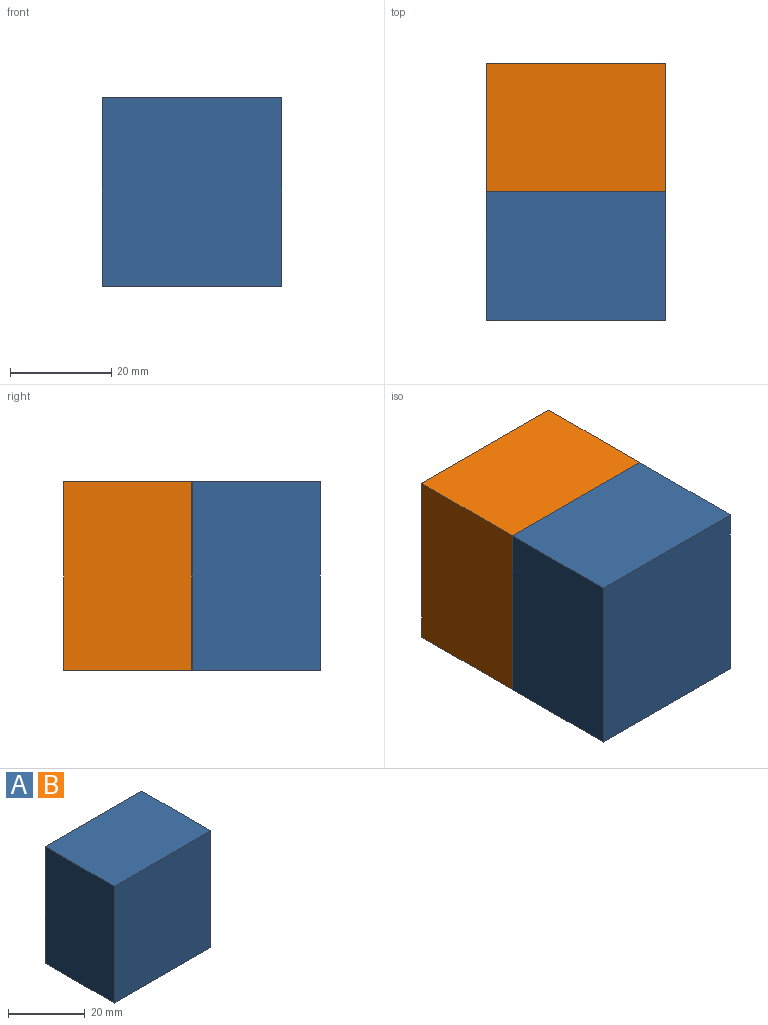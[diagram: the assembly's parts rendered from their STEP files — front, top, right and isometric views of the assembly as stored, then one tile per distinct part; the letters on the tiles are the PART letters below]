
ASSEMBLY  parts=2 mates=1
PART A: 6 faces, bbox 35.5x25.4x37.2 mm
  f0: plane 35.52x25.4mm, normal (0,0,-1), area 902.3mm2, adj f1,f3,f4,f5
  f1: plane 37.22x25.4mm, normal (1,0,0), area 945.4mm2, adj f0,f2,f4,f5
  f2: plane 35.52x25.4mm, normal (0,0,1), area 902.3mm2, adj f1,f3,f4,f5
  f3: plane 37.22x25.4mm, normal (-1,0,0), area 945.4mm2, adj f0,f2,f4,f5
  f4: plane 37.22x35.52mm, normal (0,-1,0), area 1322.2mm2, adj f0,f1,f2,f3
  f5: plane 37.22x35.52mm, normal (0,1,0), area 1322.2mm2, adj f0,f1,f2,f3
PART B: same geometry as A
PLACE A rot(axis=(1,0,0),180deg) t=(64.43,-5,13.21)mm
PLACE B t=(64.43,45.8,12.9)mm
MATE revolute A.f4 <-> B.f4  axis (0,1,0) through (-63.99,20.4,13.05)mm
